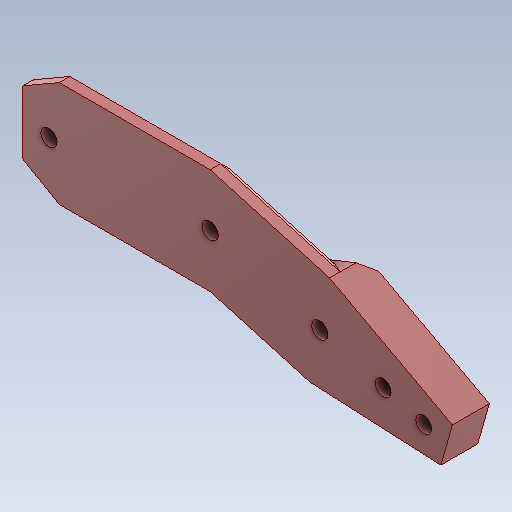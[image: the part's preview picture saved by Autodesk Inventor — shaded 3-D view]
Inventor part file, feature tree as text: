
AUTODESK INVENTOR PART (.ipt)
format: ipt  version: 2020 (Build 240168000, 168)  size: 181,248 bytes
history: native  units: in
note: dims shown in document units (in); Inventor stores cm internally (conversion verified against a paired STEP export)
features: sketch x4, other x3
ambient origin geometry x8: Origin, YZ Plane, XZ Plane, XY Plane, X Axis, Y Axis, Z Axis, Center Point
bodies: Solid1 (feature_tree)
feature tree (7):
  other  "FibulaBot.ipt"
  other  "Solid1::FibulaBot.ipt"
  other  "TaggingFeature1"
  sketch  "Sketch1"  dims[d0=0.3937in]
  sketch  "Sketch3"
  sketch  "Sketch4"
  sketch  "Sketch5"
